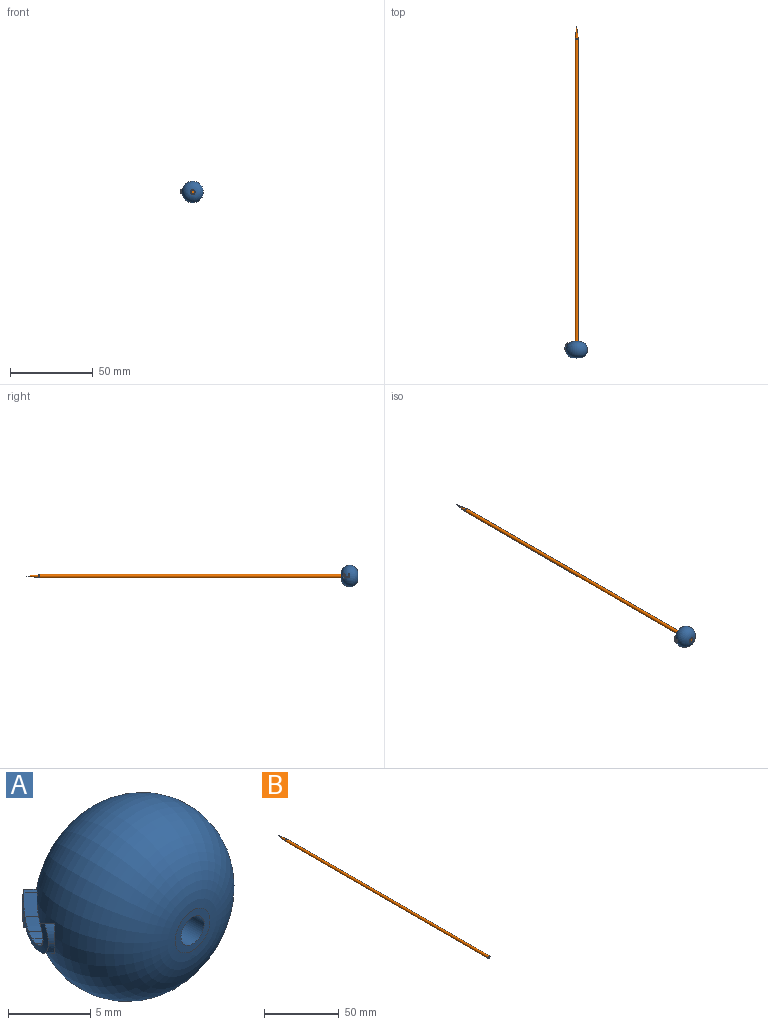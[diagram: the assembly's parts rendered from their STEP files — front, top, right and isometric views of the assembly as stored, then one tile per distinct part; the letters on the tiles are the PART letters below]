
ASSEMBLY  parts=2 mates=1
PART A: 26 faces, bbox 14.1x10x11.5 mm
  f0: plane 0.59x0.59mm, normal (0,0,-1), area 0mm2, adj f1,f13,f21,f25
  f1: plane 1.25x1.1mm, normal (0.51,0.51,-0.7), area 1mm2, adj f0,f2,f21,f25
  f2: extruded ~1.53x1.53mm, area 1mm2, adj f1,f3,f21,f25
  f3: extruded ~1.51x1.51mm, area 0.7mm2, adj f2,f4,f21,f25
  f4: extruded ~1.31x1.31mm, area 0.7mm2, adj f3,f14,f15,f21,f25
  f5: extruded ~1.18x1.18mm, area 0.5mm2, adj f6,f14,f20,f21,f25
  f6: extruded ~1.14x1.14mm, area 0.4mm2, adj f5,f7,f21,f25
  f7: extruded ~1.06x1.06mm, area 0.4mm2, adj f6,f8,f21,f25
  f8: extruded ~1.26x1.26mm, area 0.8mm2, adj f7,f9,f21,f25
  f9: plane 1.37x1.27mm, normal (-0.5,-0.5,0.71), area 1.2mm2, adj f8,f10,f21,f25
  f10: plane 0.87x0.84mm, normal (0,0,1), area 0.3mm2, adj f9,f11,f21,f25
  f11: plane 2.59x0.66mm, normal (0.71,0.71,0), area 2.1mm2, adj f10,f12,f21,f25
  f12: plane 0.89x0.86mm, normal (0,0,-1), area 0.3mm2, adj f11,f13,f21,f25
  f13: plane 2.03x0.65mm, normal (-0.71,-0.71,0), area 1.6mm2, adj f0,f12,f21,f25
  f14: plane 2.38x0.68mm, normal (0.71,-0.71,0), area 1mm2, adj f4,f5,f15,f16,f17,f18,f19,f20
  f15: extruded ~0.87x0.61mm, area 0.4mm2, adj f4,f14,f16,f21
  f16: extruded ~1.19x0.76mm, area 0.7mm2, adj f14,f15,f17,f21
  f17: plane 0.86x0.66mm, normal (0.43,0.43,0.79), area 0.3mm2, adj f14,f16,f18,f21
  f18: extruded ~0.85x0.85mm, area 0.5mm2, adj f14,f17,f19,f21
  f19: extruded ~0.59x0.59mm, area 0.3mm2, adj f14,f18,f20,f21
  f20: extruded ~0.73x0.73mm, area 0.4mm2, adj f5,f14,f19,f21
  f21: torus R=1.5mm, axis (0,-1,0), area 3.8mm2, adj f0,f1,f2,f3,f4,f5,f6,f7
  f22: cylinder r=1mm len=10mm, axis (0,1,0), area 62.8mm2, adj f23,f24
  f23: plane 3x3mm, normal (0,-1,0), area 3.9mm2, adj f22,f25
  f24: plane 3x3mm, normal (0,1,0), area 3.9mm2, adj f22,f25
  f25: torus R=1.5mm, axis (0,-1,0), area 459.6mm2, adj f0,f1,f2,f3,f4,f5,f6,f7
PART B: 4 faces, bbox 2x200x2 mm
  f0: cylinder r=1mm len=191.69mm, axis (0,1,0), area 1204.4mm2, adj f1,f3
  f1: plane 2x2mm, normal (0,-1,0), area 3.1mm2, adj f0
  f2: cone r=1mm half-angle=7.1deg, axis (0,-1,0), area 23.4mm2, adj f3
  f3: revolved ~2x2mm, area 3.9mm2, adj f0,f2
PLACE A t=(-5.69,1.15,-0.47)mm fixed
PLACE B t=(-5.69,183.15,-0.47)mm
MATE fastened B.f0 <-> A.f21  axis (0,1,0) through (-5.69,-8.85,-0.47)mm
